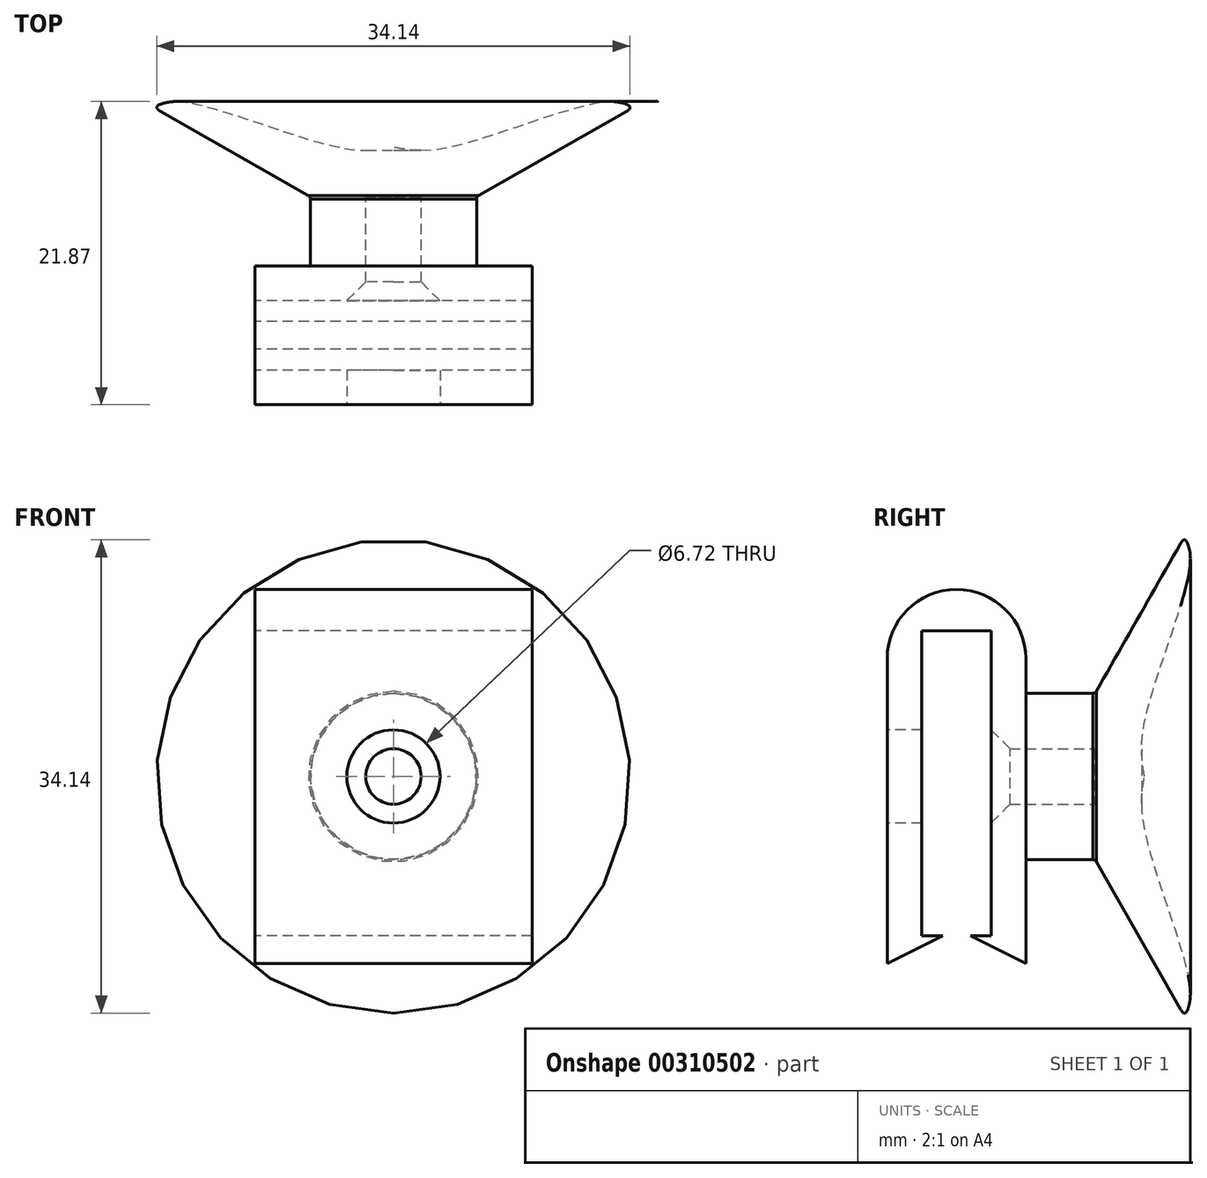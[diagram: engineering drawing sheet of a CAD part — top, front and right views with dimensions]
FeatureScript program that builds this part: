
annotation { "Feature Type Name" : "Feature", "Feature Type Description" : "" }
export const myFeature = defineFeature(function(context is Context, id is Id, definition is map)
    precondition{}
    {
        {
            var Q0;
            Q0=qCreatedBy(makeId("Right.planeOp"),FACE);
            var sketch = newSketch(context, id + "F0", { "sketchPlane" : qUnion([Q0])});
            skLineSegment(sketch, "E0.bottom", {"start": v(0, 0) * mm, "end": v(10, 0) * mm});
            skLineSegment(sketch, "E0.top", {"start": v(0, 27) * mm, "end": v(10, 27) * mm});
            skLineSegment(sketch, "E0.left", {"start": v(0, 0) * mm, "end": v(0, 27) * mm});
            skLineSegment(sketch, "E0.right", {"start": v(10, 0) * mm, "end": v(10, 27) * mm});
            skLineSegment(sketch, "E1", {"start": v(2.5, 24) * mm, "end": v(2.5, 2) * mm});
            skLineSegment(sketch, "E2", {"start": v(7.5, 2) * mm, "end": v(7.5, 24) * mm});
            skLineSegment(sketch, "E3", {"start": v(2.5, 24) * mm, "end": v(7.5, 24) * mm});
            skLineSegment(sketch, "E4", {"start": v(2.5, 2) * mm, "end": v(4, 2) * mm});
            skLineSegment(sketch, "E5", {"start": v(4, 2) * mm, "end": v(0, 0) * mm});
            skLineSegment(sketch, "E6", {"start": v(7.5, 2) * mm, "end": v(6, 2) * mm});
            skLineSegment(sketch, "E7", {"start": v(6, 2) * mm, "end": v(10, 0) * mm});
            skLineSegment(sketch, "E8", {"start": v(5, 27) * mm, "end": v(5, 2.65) * mm, "construction": true});
            skSolve(sketch);
        }
        {
            var Q0;
            Q0=makeQuery(id+"F0.imprint","IMPRINT",FACE,{"disambiguationData":[TD([[makeQuery(id+"F0.imprint","IMPRINT",EDGE,{"derivedFrom":sQuery(id+"F0.wireOp",EDGE,"E0.top")}),-1.0]])]});
            extrude(context, id + "F1", {"entities" : qUnion([Q0]), "depth" : 20 * mm});
        }
        {
            var Q0;
            Q0=makeQuery(id+"F1.opExtrude","SWEPT_FACE",FACE,{"disambiguationData":[OSD([sQuery(id+"F0.wireOp",EDGE,"E0.right")])]});
            cPlane(context, id + "F2", {"entities" : qUnion([Q0]), "cplaneType" : CPlaneType.OFFSET, "offset" : 5 * mm, "width" : 150 * mm, "height" : 150 * mm});
        }
        {
            var Q0;
            Q0=qCreatedBy(id+"F2.planeOp",FACE);
            var sketch = newSketch(context, id + "F3", { "sketchPlane" : qUnion([Q0])});
            skCircle(sketch, "E9", {"center": v(-10, 13.5) * mm, "radius": 6 * mm});
            skPoint(sketch, "E9.centerSnap0", {"position": v(-20, 13.5) * mm});
            skPoint(sketch, "E9.centerSnap1", {"position": v(-10, 27) * mm});
            skCircle(sketch, "E10", {"center": v(-10, 13.5) * mm, "radius": 2 * mm});
            skLineSegment(sketch, "E11.0.0", {"start": v(0, 0) * mm, "end": v(0, 27) * mm});
            skLineSegment(sketch, "E11.0.1", {"start": v(0, 27) * mm, "end": v(-20, 27) * mm});
            skLineSegment(sketch, "E11.0.2", {"start": v(-20, 27) * mm, "end": v(-20, 0) * mm});
            skLineSegment(sketch, "E11.0.3", {"start": v(-20, 0) * mm, "end": v(0, 0) * mm});
            skSolve(sketch);
        }
        {
            var Q0;
            Q0=makeQuery(id+"F3.imprint","IMPRINT",FACE,{"disambiguationData":[TD([[makeQuery(id+"F3.imprint","IMPRINT",EDGE,{"derivedFrom":sQuery(id+"F3.wireOp",EDGE,"E10")}),1.0]])]});
            var Q1;
            Q1=makeQuery(id+"F3.imprint","IMPRINT",FACE,{"disambiguationData":[TD([[makeQuery(id+"F3.imprint","IMPRINT",EDGE,{"derivedFrom":sQuery(id+"F3.wireOp",EDGE,"E9")}),1.0]])]});
            extrude(context, id + "F4", {"entities" : qUnion([Q0, Q1]), "operationType" : NewBodyOperationType.ADD, "oppositeDirection" : true, "depth" : 5 * mm});
        }
        {
            var Q0;
            Q0=makeQuery(id+"F3.imprint","IMPRINT",FACE,{"disambiguationData":[TD([[makeQuery(id+"F3.imprint","IMPRINT",EDGE,{"derivedFrom":sQuery(id+"F3.wireOp",EDGE,"E10")}),1.0]])]});
            extrude(context, id + "F5", {"entities" : qUnion([Q0]), "operationType" : NewBodyOperationType.REMOVE, "oppositeDirection" : true, "depth" : 25 * mm});
        }
        {
            var Q0;
            Q0=makeQuery(id+"F1.opExtrude","SWEPT_EDGE",EDGE,{"disambiguationData":[OSD([sQuery(id+"F0.wireOp",EDGE,"E0.top"),sQuery(id+"F0.wireOp",EDGE,"E0.right")])]});
            var Q1;
            Q1=makeQuery(id+"F1.opExtrude","SWEPT_EDGE",EDGE,{"disambiguationData":[OSD([sQuery(id+"F0.wireOp",EDGE,"E0.top"),sQuery(id+"F0.wireOp",EDGE,"E0.left")])]});
            fillet(context, id + "F6", {"entities" : qUnion([Q0, Q1]), "radius" : 5 * mm, "tangentPropagation" : true, "allowEdgeOverflow" : false});
        }
        {
            var Q0;
            Q0=makeQuery(id+"F1.opExtrude","SWEPT_FACE",FACE,{"disambiguationData":[OSD([sQuery(id+"F0.wireOp",EDGE,"E2")])]});
            var sketch = newSketch(context, id + "F7", { "sketchPlane" : qUnion([Q0])});
            skCircle(sketch, "E12.0", {"center": v(10, 13.5) * mm, "radius": 2 * mm});
            skSolve(sketch);
        }
        {
            var Q0;
            Q0=sQuery(id+"F7.wireOp",VERTEX,"E12.0.center");
            var Q1;
            Q1=makeQuery(id+"F1.opExtrude","SWEPT_BODY",BODY,{"disambiguationData":[OSD([sQuery(id+"F0.wireOp",EDGE,"E0.top"),sQuery(id+"F0.wireOp",EDGE,"E0.left"),sQuery(id+"F0.wireOp",EDGE,"E0.right"),sQuery(id+"F0.wireOp",EDGE,"E1"),sQuery(id+"F0.wireOp",EDGE,"E2"),sQuery(id+"F0.wireOp",EDGE,"E3"),sQuery(id+"F0.wireOp",EDGE,"E4"),sQuery(id+"F0.wireOp",EDGE,"E5"),sQuery(id+"F0.wireOp",EDGE,"E6"),sQuery(id+"F0.wireOp",EDGE,"E7")])]});
            hole(context, id + "F8", {"style" : HoleStyle.C_SINK, "endStyle" : HoleEndStyle.BLIND, "standardTappedOrClearance" : lookupTablePath({ "standard" : "ISO", "fit" : "Normal", "size" : "M3", "type" : "Clearance" }), "standardBlindInLast" : lookupTablePath({ "fit" : "Standard", "standard" : "ISO", "size" : "M3", "type" : "Clearance" }), "holeDiameter" : 3.3 * mm, "cSinkDiameter" : 6.72 * mm, "cSinkAngle" : 90 * degree, "holeDepth" : 13.5 * mm, "isTappedThrough" : true, "tappedDepth" : 12 * mm, "tapClearance" : 3, "locations" : qUnion([Q0]), "scope" : qUnion([Q1])});
        }
        {
            var Q0;
            Q0=makeQuery(id+"F1.opExtrude","SWEPT_FACE",FACE,{"disambiguationData":[OSD([sQuery(id+"F0.wireOp",EDGE,"E0.left")])]});
            var sketch = newSketch(context, id + "F9", { "sketchPlane" : qUnion([Q0])});
            skCircle(sketch, "E13.0", {"center": v(10, 13.5) * mm, "radius": 3.36 * mm});
            skSolve(sketch);
        }
        {
            var Q0;
            Q0=makeQuery(id+"F9.imprint","IMPRINT",FACE,{"disambiguationData":[TD([[makeQuery(id+"F9.imprint","IMPRINT",EDGE,{"derivedFrom":sQuery(id+"F9.wireOp",EDGE,"E13.0")}),1.0]])]});
            extrude(context, id + "F10", {"entities" : qUnion([Q0]), "operationType" : NewBodyOperationType.REMOVE, "endBound" : BoundingType.UP_TO_NEXT, "oppositeDirection" : true, "depth" : 25 * mm, "offsetDistance" : 25 * mm});
        }
        {
            var Q0;
            Q0=makeQuery(id+"F3.imprint","IMPRINT",FACE,{"disambiguationData":[TD([[makeQuery(id+"F3.imprint","IMPRINT",EDGE,{"derivedFrom":sQuery(id+"F3.wireOp",EDGE,"E9")}),1.0]])]});
            var sketch = newSketch(context, id + "F11", { "sketchPlane" : qUnion([Q0])});
            skCircle(sketch, "E14.0", {"center": v(-10, 13.5) * mm, "radius": 6 * mm});
            skCircle(sketch, "E14.1", {"center": v(-10, 13.5) * mm, "radius": 2 * mm});
            skSolve(sketch);
        }
        {
            var Q0;
            Q0=sQuery(id+"F3.wireOp",VERTEX,"E9.center");
            var Q1;
            Q1=qCreatedBy(makeId("Right.planeOp"),FACE);
            cPlane(context, id + "F12", {"entities" : qUnion([Q0, Q1]), "cplaneType" : CPlaneType.PLANE_POINT, "offset" : 25 * mm, "width" : 150 * mm, "height" : 150 * mm});
        }
        {
            var Q0;
            Q0=qCreatedBy(id+"F12.planeOp",FACE);
            var sketch = newSketch(context, id + "F13", { "sketchPlane" : qUnion([Q0])});
            skLineSegment(sketch, "E15", {"start": v(15, 13.5) * mm, "end": v(18.57, 13.5) * mm});
            skLineSegment(sketch, "E16", {"start": v(21.46, 30.83) * mm, "end": v(15, 19.5) * mm});
            skLineSegment(sketch, "E17", {"start": v(15, 19.5) * mm, "end": v(15, 13.5) * mm});
            skFitSpline(sketch, "E18", {"points": [v(18.57, 13.5) * mm, v(18.57, 17.43) * mm, v(21.83, 28.58) * mm, v(21.46, 30.83) * mm], "startDerivative": vector(-1.96, 10.97) * mm, "endDerivative": vector(-3.5, 7.67) * mm});
            skSolve(sketch);
        }
        {
            var Q0;
            Q0=makeQuery(id+"F13.imprint","IMPRINT",FACE,{"disambiguationData":[TD([[makeQuery(id+"F13.imprint","IMPRINT",EDGE,{"derivedFrom":sQuery(id+"F13.wireOp",EDGE,"E15")}),1.0]])]});
            var Q1;
            Q1=sQuery(id+"F13.wireOp",EDGE,"E15");
            revolve(context, id + "F14", {"operationType" : NewBodyOperationType.ADD, "entities" : qUnion([Q0]), "axis" : qUnion([Q1]), "revolveType" : RevolveType.FULL});
        }
        {
            var Q0;
            Q0=makeQuery(id+"F14.opRevolve","SWEPT_EDGE",EDGE,{"disambiguationData":[OSD([sQuery(id+"F13.wireOp",EDGE,"yK5iJPrr-65jA-vMDR-mDNz-eyCEgEZsFUvv"),sQuery(id+"F13.wireOp",EDGE,"E16")])]});
            fillet(context, id + "F15", {"entities" : qUnion([Q0]), "radius" : 0.3 * mm, "tangentPropagation" : true, "rho" : 0.5, "crossSection" : FilletCrossSection.CONIC, "allowEdgeOverflow" : false});
        }
    });
